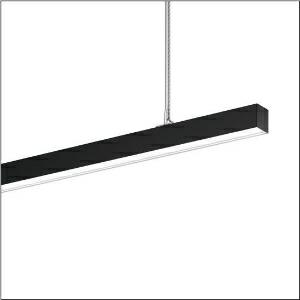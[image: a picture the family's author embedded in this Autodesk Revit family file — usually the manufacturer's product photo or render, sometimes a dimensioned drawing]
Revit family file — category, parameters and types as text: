
# Revit family: silica_r__21_51mx30dc39bb_25b6
name_source: partatom
category: Lighting Fixtures
units: mm (PartAtom-declared; Revit-internal decimal feet)

## family parameters
Cut with Voids When Loaded = No
Host = Face
Light Source = No
Part Type = Normal
Room Calculation Point = No
Round Connector Dimension = Use Diameter
Shared = No

## types (1)
- --- (1 x LED, 10520 lm, 68.3 W, 3000K)
    Apparent Load = 68 VA
    CIE Flux Codes = 47 79 96 57 100
    Color Rendering = 80
    Color Temperature = 3000K
    Default Elevation = 1800 mm
    Description = Silica® 21, office luminaire, primary optical cover: cover, of PMMA, opal, light emission: direct/indirect distribution, primary light characteristic: symmetric, installation type: suspended mounting, LED, rated luminous flux: 10.520lm, luminous efficacy: 154lm/W, light colour: 830, colour temperature: 3000K, with terminal, 3+2-pole, max. 2.5mm², mains connection: 220..240V, AC, 50/60Hz, rated input power: 68.3W, luminaire housing, of aluminium, jet black (RAL 9005), length: 3.004mm, width: 53mm, height: 53mm, protection rating (complete): IP20, insulation class (complete): insulation class I (protective earthing), certification: CE, permissible operating ambient temperature: 0..+35°C, standard: EN 50419, packaging unit: 1 piece
    Height = 53 mm
    Lamp = 1 x LED
    Lamp Light Flux = 10520 lm
    Lamp Power = 68.3 W
    Lamp count = 1
    Length = 3004 mm
    Luminous efficacy = 154 lm/W
    Manufacturer = Siteco
    ModVariant = No
    Model = 51MX30DC39BB
    Mounting Place = Ceiling
    Mounting Type = Pendant
    Number of Poles = 1
    OnlyDefault = Yes
    Power Factor = 1
    Product Name = Silica® 21
    Product group = office luminaire | ceiling pendant
    ProductGroupID = 905
    Protection Class = Protection class I
    Protection Degree = IP 20
    RLX_Detail_Level = 1
    RlxData = <blob elided: 26093 chars, md5=e36d32c3>
    Socket = socket
    Standby Power = 0 W
    System Light Flux = 10520 lm
    System Power = 68 W
    Type Comments = factory setting: luminous flux: 100 % | dim-lin: 254 | 233 mA
    Type Image = l_1251735.jpg
    URL = http://relux.com
    VarID = @adj_025629
    Voltage = 0 V
    Weight = 0.00 kg
    Width = 53 mm

## geometry (parser evidence)
native form markers: Blend x4, Sweep x13
no freeform markers — native parametric forms only
